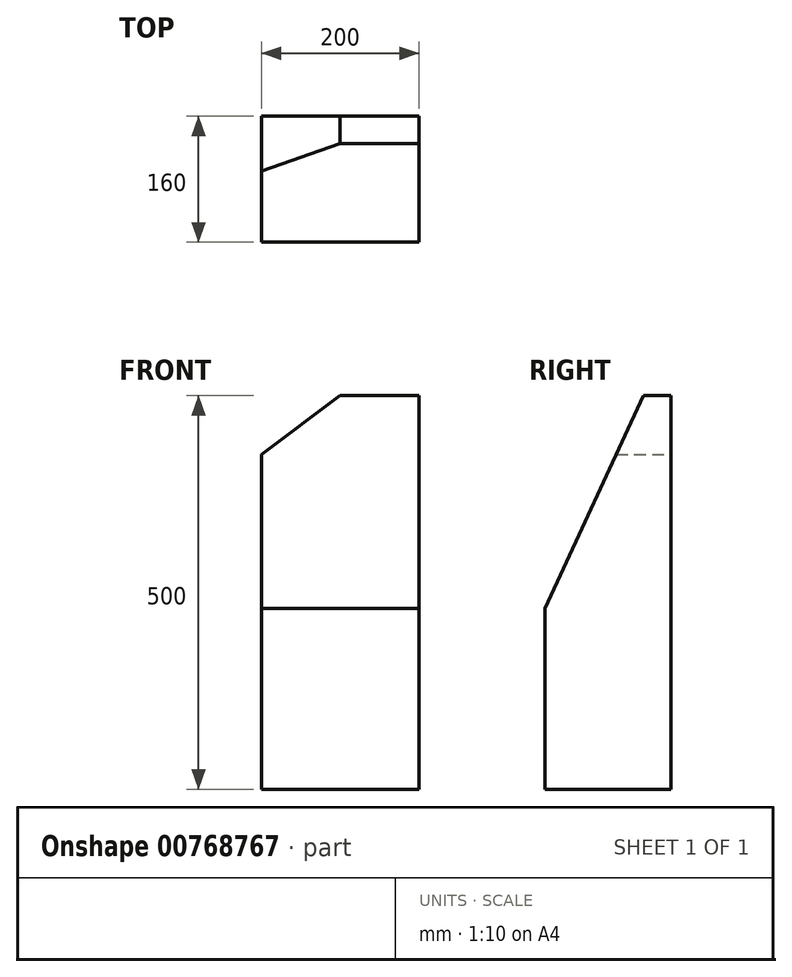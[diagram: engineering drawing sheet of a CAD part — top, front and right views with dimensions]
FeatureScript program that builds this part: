
annotation { "Feature Type Name" : "Feature", "Feature Type Description" : "" }
export const myFeature = defineFeature(function(context is Context, id is Id, definition is map)
    precondition{}
    {
        {
            var Q0;
            Q0=qCreatedBy(makeId("Top.planeOp"),FACE);
            var sketch = newSketch(context, id + "F0", { "sketchPlane" : qUnion([Q0])});
            skLineSegment(sketch, "E0.bottom", {"start": v(0, 0) * mm, "end": v(-200, 0) * mm});
            skLineSegment(sketch, "E0.top", {"start": v(0, -160) * mm, "end": v(-200, -160) * mm});
            skLineSegment(sketch, "E0.left", {"start": v(0, 0) * mm, "end": v(0, -160) * mm});
            skLineSegment(sketch, "E0.right", {"start": v(-200, 0) * mm, "end": v(-200, -160) * mm});
            skSolve(sketch);
        }
        {
            var Q0;
            Q0=makeQuery(id+"F0.imprint","IMPRINT",FACE,{"disambiguationData":[TD([[makeQuery(id+"F0.imprint","IMPRINT",EDGE,{"derivedFrom":sQuery(id+"F0.wireOp",EDGE,"E0.bottom")}),1.0]])]});
            extrude(context, id + "F1", {"entities" : qUnion([Q0]), "depth" : 500 * mm, "offsetDistance" : 25 * mm});
        }
        {
            var Q0;
            Q0=makeQuery(id+"F1.opExtrude","CAP_EDGE",EDGE,{"disambiguationData":[OSD([sQuery(id+"F0.wireOp",EDGE,"E0.right")])],"isStart":false});
            chamfer(context, id + "F2", {"entities" : qUnion([Q0]), "chamferType" : ChamferType.TWO_OFFSETS, "width1" : 100 * mm, "oppositeDirection" : false, "width2" : 75 * mm, "tangentPropagation" : true});
        }
        {
            var Q0;
            Q0=makeQuery(id+"F1.opExtrude","CAP_EDGE",EDGE,{"disambiguationData":[OSD([sQuery(id+"F0.wireOp",EDGE,"E0.top")])],"isStart":false});
            chamfer(context, id + "F3", {"entities" : qUnion([Q0]), "chamferType" : ChamferType.TWO_OFFSETS, "width1" : 125 * mm, "oppositeDirection" : true, "width2" : 270 * mm, "tangentPropagation" : true});
        }
    });
